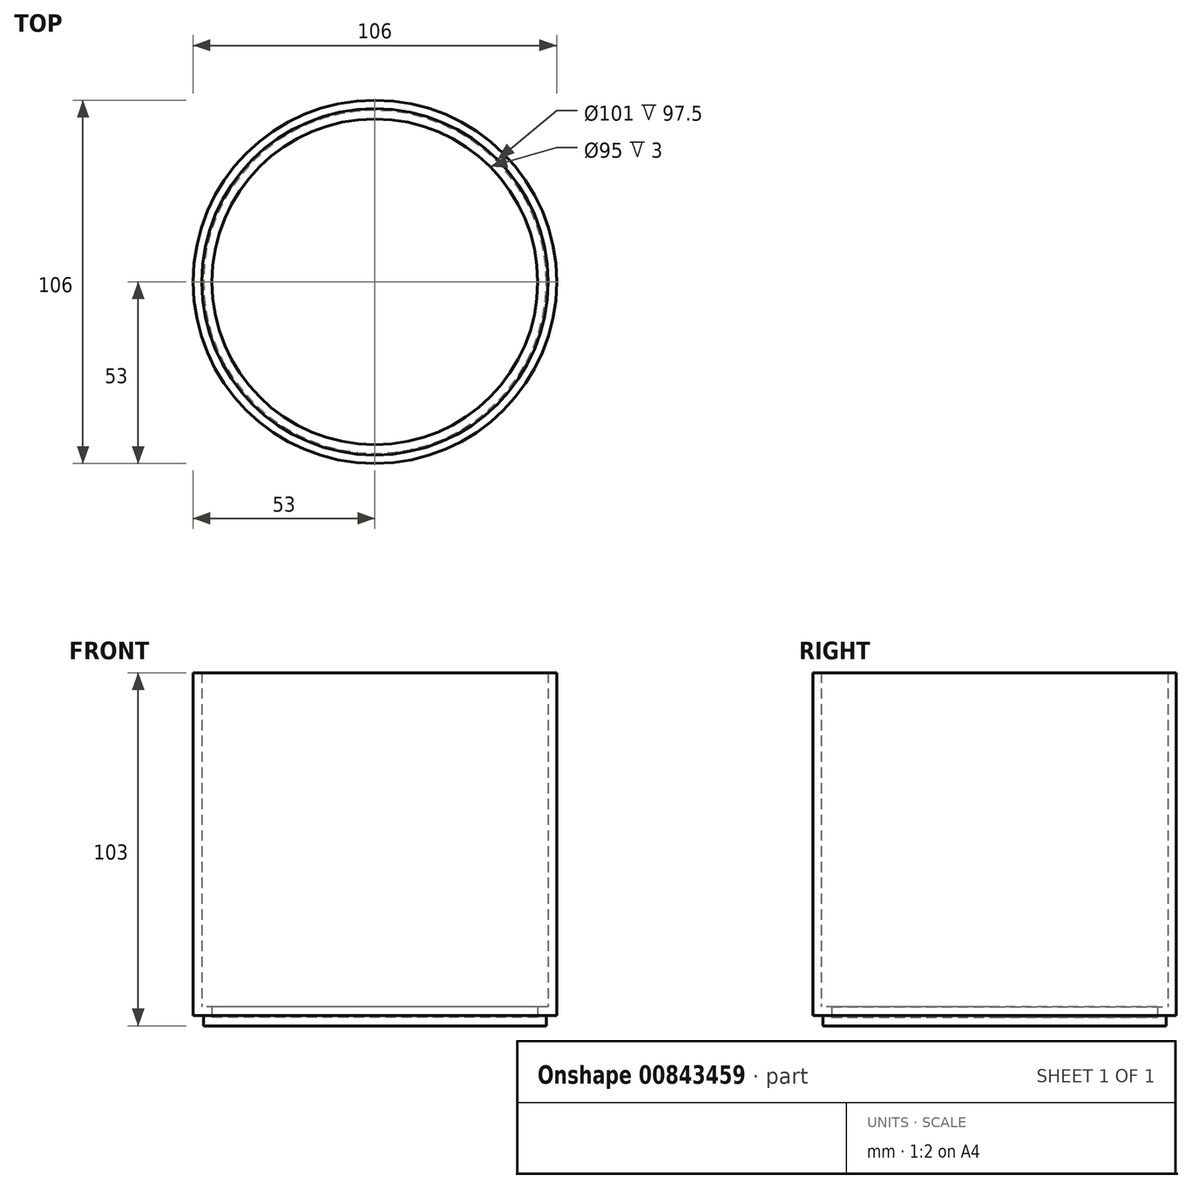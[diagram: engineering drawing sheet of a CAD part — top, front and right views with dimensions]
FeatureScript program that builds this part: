
annotation { "Feature Type Name" : "Feature", "Feature Type Description" : "" }
export const myFeature = defineFeature(function(context is Context, id is Id, definition is map)
    precondition{}
    {
        {
            var Q0;
            Q0=qCreatedBy(makeId("Front.planeOp"),FACE);
            var sketch = newSketch(context, id + "F0", { "sketchPlane" : qUnion([Q0])});
            skLineSegment(sketch, "E0", {"start": v(-343.16, 11.83) * mm, "end": v(-343.16, -88.17) * mm});
            skLineSegment(sketch, "E1", {"start": v(-343.16, -88.17) * mm, "end": v(-346.16, -88.17) * mm});
            skLineSegment(sketch, "E2", {"start": v(-346.16, -88.17) * mm, "end": v(-346.16, -91.17) * mm});
            skLineSegment(sketch, "E3", {"start": v(-346.16, -91.17) * mm, "end": v(-396.16, -91.17) * mm});
            skLineSegment(sketch, "E4", {"start": v(-396.16, -91.17) * mm, "end": v(-396.16, 11.83) * mm});
            skLineSegment(sketch, "E5", {"start": v(-396.16, 11.83) * mm, "end": v(-343.16, 11.83) * mm});
            skLineSegment(sketch, "E6", {"start": v(-343.16, 11.83) * mm, "end": v(-227.65, 11.83) * mm});
            skLineSegment(sketch, "E7", {"start": v(-227.65, 11.83) * mm, "end": v(-225.6, -132.3) * mm});
            skLineSegment(sketch, "E8", {"start": v(-225.6, -132.3) * mm, "end": v(-396.16, -134.71) * mm});
            skLineSegment(sketch, "E9", {"start": v(-396.16, -134.71) * mm, "end": v(-396.16, -91.17) * mm});
            skSolve(sketch);
        }
        {
            var Q0;
            Q0=makeQuery(id+"F0.imprint","IMPRINT",FACE,{"disambiguationData":[TD([[makeQuery(id+"F0.imprint","IMPRINT",EDGE,{"derivedFrom":sQuery(id+"F0.wireOp",EDGE,"E0")}),-1.0]])]});
            var Q1;
            Q1=sQuery(id+"F0.wireOp",EDGE,"E4");
            revolve(context, id + "F1", {"surfaceOperationType" : NewSurfaceOperationType.NEW, "entities" : qUnion([Q0]), "axis" : qUnion([Q1]), "revolveType" : RevolveType.FULL});
        }
        {
            var Q0;
            Q0=makeQuery(id+"F1.opRevolve","SWEPT_FACE",FACE,{"disambiguationData":[OSD([sQuery(id+"F0.wireOp",EDGE,"E5")])]});
            shell(context, id + "F2", {"entities" : qUnion([Q0]), "thickness" : 2.5 * mm});
        }
    });
